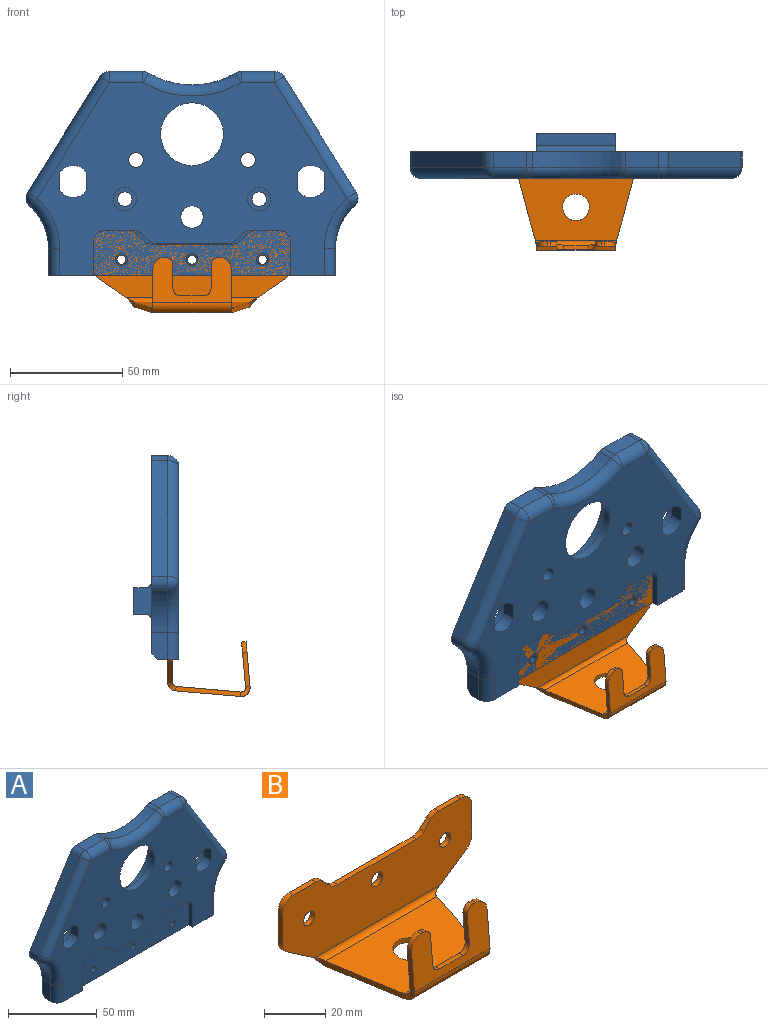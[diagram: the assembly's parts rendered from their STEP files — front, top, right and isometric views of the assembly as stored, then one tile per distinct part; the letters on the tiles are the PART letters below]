
ASSEMBLY  parts=2 mates=1
PART A: 140 faces, bbox 148.2x20x91 mm
  f0: plane 7.27x6mm, normal (-1,0,0), area 43.6mm2, adj f1,f9,f11,f79
  f1: cylinder r=7.1mm len=12.2mm, axis (0,1,0), area 88.1mm2, adj f0,f2,f11,f79
  f2: plane 7.27x6mm, normal (1,0,0), area 43.6mm2, adj f1,f9,f11,f79
  f3: cylinder r=7.1mm len=12.02mm, axis (0,1,0), area 86mm2, adj f4,f8,f11,f107
  f4: plane 7.56x6mm, normal (-1,0,0), area 45.4mm2, adj f3,f5,f11,f107
  f5: cylinder r=7.1mm len=12.02mm, axis (0,1,0), area 86mm2, adj f4,f8,f11,f107
  f6: cylinder r=3.25mm len=12mm, axis (0,1,0), area 196mm2, adj f10,f11,f89,f90,f96
  f7: cylinder r=3.25mm len=12mm, axis (0,1,0), area 196mm2, adj f10,f11,f97,f98,f105
  f8: plane 7.56x6mm, normal (1,0,0), area 45.4mm2, adj f3,f5,f11,f107
  f9: cylinder r=7.1mm len=12.2mm, axis (0,1,0), area 88.1mm2, adj f0,f2,f11,f79
  f10: plane 148.17x88.5mm, normal (0,1,0), area 4917.2mm2, adj f6,f7,f12,f13,f15,f16,f17,f19
  f11: plane 138.17x86mm, normal (0,-1,0), area 6760.8mm2, adj f0,f1,f2,f3,f4,f5,f6,f7
  f12: cylinder r=3.25mm len=6.5mm, axis (0,1,0), area 122.5mm2, adj f10,f30
  f13: cylinder r=3.25mm len=6.5mm, axis (0,1,0), area 122.5mm2, adj f10,f28
  f14: cylinder r=14mm len=28mm, axis (0,1,0), area 351.9mm2, adj f11,f26
  f15: plane 51.56x32.22mm, normal (-0.85,0,0.53), area 425.6mm2, adj f10,f31,f36,f40
  f16: cylinder r=25mm len=18.7mm, axis (0,1,0), area 147.8mm2, adj f10,f17,f31,f38
  f17: plane 12x7mm, normal (-1,0,0), area 80.9mm2, adj f10,f16,f18,f37,f59
  f18: plane 128x9.5mm, normal (0,0,-1), area 941.3mm2, adj f11,f17,f19,f37,f51,f59,f60,f61
  f19: plane 12x7mm, normal (1,0,0), area 80.9mm2, adj f10,f18,f20,f51,f59
  f20: cylinder r=25mm len=18.7mm, axis (0,1,0), area 147.8mm2, adj f10,f19,f32,f50
  f21: plane 51.56x32.22mm, normal (0.85,0,0.53), area 425.6mm2, adj f10,f32,f33,f48
  f22: plane 14.96x7mm, normal (0,0,1), area 104.7mm2, adj f10,f33,f34,f46
  f23: cylinder r=38mm len=38.72mm, axis (0,1,0), area 284.4mm2, adj f10,f34,f35,f44
  f24: plane 14.96x7mm, normal (0,0,1), area 104.7mm2, adj f10,f35,f36,f42
  f25: cylinder r=21mm len=42mm, axis (0,1,0), area 1055.6mm2, adj f10,f26
  f26: plane 42x42mm, normal (0,1,0), area 769.7mm2, adj f14,f25
  f27: cylinder r=5.25mm len=10.5mm, axis (0,-1,0), area 197.9mm2, adj f11,f28
  f28: plane 10.5x10.5mm, normal (0,-1,0), area 53.4mm2, adj f13,f27
  f29: cylinder r=5.25mm len=10.5mm, axis (0,-1,0), area 197.9mm2, adj f11,f30
  f30: plane 10.5x10.5mm, normal (0,-1,0), area 53.4mm2, adj f12,f29
  f31: cylinder r=5mm len=7mm, axis (0,1,0), area 49.1mm2, adj f10,f15,f16,f39
  f32: cylinder r=5mm len=7mm, axis (0,1,0), area 49.1mm2, adj f10,f20,f21,f49
  f33: cylinder r=5mm len=7mm, axis (0,1,0), area 35.4mm2, adj f10,f21,f22,f47
  f34: cylinder r=5mm len=7mm, axis (0,1,0), area 18.7mm2, adj f10,f22,f23,f45
  f35: cylinder r=5mm len=7mm, axis (0,1,0), area 18.7mm2, adj f10,f23,f24,f43
  f36: cylinder r=5mm len=7mm, axis (0,1,0), area 35.4mm2, adj f10,f15,f24,f41
  f37: cylinder r=5mm len=12mm, axis (0,0,1), area 94.2mm2, adj f11,f17,f18,f38
  f38: torus R=30mm, axis (0,-1,0), area 177.9mm2, adj f11,f16,f37,f39
  f39: sphere r=5mm, area 35.1mm2, adj f31,f38,f40
  f40: cylinder r=5mm len=54.21mm, axis (0.53,0,0.85), area 477.5mm2, adj f11,f15,f39,f41
  f41: sphere r=5mm, area 25.3mm2, adj f36,f40,f42
  f42: cylinder r=5mm len=14.96mm, axis (1,0,0), area 117.5mm2, adj f11,f24,f41,f43
  f43: sphere r=5mm, area 13.4mm2, adj f35,f42,f44
  f44: torus R=43mm, axis (0,-1,0), area 334.4mm2, adj f11,f23,f43,f45
  f45: sphere r=5mm, area 13.4mm2, adj f34,f44,f46
  f46: cylinder r=5mm len=14.96mm, axis (1,0,0), area 117.5mm2, adj f11,f22,f45,f47
  f47: sphere r=5mm, area 25.3mm2, adj f33,f46,f48
  f48: cylinder r=5mm len=54.21mm, axis (0.53,0,-0.85), area 477.5mm2, adj f11,f21,f47,f49
  f49: sphere r=5mm, area 35.1mm2, adj f32,f48,f50
  f50: torus R=30mm, axis (0,-1,0), area 177.9mm2, adj f11,f20,f49,f51
  f51: cylinder r=5mm len=12mm, axis (0,0,-1), area 94.2mm2, adj f11,f18,f19,f50
  f52: plane 35.5x5mm, normal (0,0,1), area 177.5mm2, adj f53,f55,f56,f58
  f53: plane 18x8mm, normal (1,0,0), area 99.9mm2, adj f10,f52,f54,f56,f57,f58
  f54: plane 35.5x5mm, normal (0,0,-1), area 177.5mm2, adj f53,f55,f56,f57
  f55: plane 18x8mm, normal (-1,0,0), area 99.9mm2, adj f10,f52,f54,f56,f57,f58
  f56: plane 35.5x12mm, normal (0,1,0), area 347.5mm2, adj f52,f53,f54,f55,f77
  f57: cylinder r=3mm len=35.5mm, axis (1,0,0), area 167.3mm2, adj f10,f53,f54,f55
  f58: cylinder r=3mm len=35.5mm, axis (-1,0,0), area 167.3mm2, adj f10,f52,f53,f55
  f59: plane 128x2.5mm, normal (0,0.71,-0.71), area 452.5mm2, adj f10,f17,f18,f19
  f60: plane 15x3mm, normal (1,0,0), area 45mm2, adj f11,f18,f67,f73
  f61: plane 15x3mm, normal (-1,0,0), area 45mm2, adj f11,f18,f67,f68
  f62: plane 12.93x3mm, normal (0,0,-1), area 38.8mm2, adj f11,f67,f68,f69
  f63: plane 3.07x3.07mm, normal (0.71,0,-0.71), area 13mm2, adj f11,f67,f69,f70
  f64: plane 31.86x3mm, normal (0,0,-1), area 95.6mm2, adj f11,f67,f70,f71
  f65: plane 3.07x3.07mm, normal (-0.71,0,-0.71), area 13mm2, adj f11,f67,f71,f72
  f66: plane 12.93x3mm, normal (0,0,-1), area 38.8mm2, adj f11,f67,f72,f73
  f67: plane 88x20mm, normal (0,-1,0), area 1459.6mm2, adj f18,f60,f61,f62,f63,f64,f65,f66
  f68: cylinder r=5mm len=5mm, axis (0,1,0), area 23.6mm2, adj f11,f61,f62,f67
  f69: cylinder r=5mm len=3.54mm, axis (0,1,0), area 11.8mm2, adj f11,f62,f63,f67
  f70: cylinder r=5mm len=3.54mm, axis (0,-1,0), area 11.8mm2, adj f11,f63,f64,f67
  f71: cylinder r=5mm len=3.54mm, axis (0,-1,0), area 11.8mm2, adj f11,f64,f65,f67
  f72: cylinder r=5mm len=3.54mm, axis (0,1,0), area 11.8mm2, adj f11,f65,f66,f67
  f73: cylinder r=5mm len=5mm, axis (0,1,0), area 23.6mm2, adj f11,f60,f66,f67
  f74: cylinder r=2mm len=9mm, axis (0,-1,0), area 113.1mm2, adj f10,f67
  f75: cylinder r=2mm len=9mm, axis (0,-1,0), area 113.1mm2, adj f10,f67
  f76: cylinder r=2mm len=9mm, axis (0,-1,0), area 113.1mm2, adj f10,f67
  f77: cylinder r=5mm len=20mm, axis (0,-1,0), area 628.3mm2, adj f11,f56
  f78: cylinder r=11.1mm len=22.2mm, axis (0,1,0), area 418.5mm2, adj f10,f79
  f79: plane 22.2x22.2mm, normal (0,1,0), area 238.5mm2, adj f0,f1,f2,f9,f78
  f80: plane 13.73x6mm, normal (1,0,0), area 82.4mm2, adj f10,f87,f116,f121
  f81: cylinder r=16mm len=6mm, axis (0,1,0), area 32.4mm2, adj f10,f87,f120,f121
  f82: plane 21.79x6mm, normal (0,0,-1), area 130.7mm2, adj f10,f87,f119,f120
  f83: plane 7.1x6mm, normal (-1,0,0), area 42.6mm2, adj f10,f87,f118,f119
  f84: plane 6x3mm, normal (0,0,1), area 18mm2, adj f10,f85,f87,f118
  f85: cylinder r=7mm len=6.64mm, axis (0,1,0), area 52.5mm2, adj f10,f84,f87,f117
  f86: plane 15.99x6mm, normal (0,0,1), area 95.9mm2, adj f10,f87,f116,f117
  f87: plane 33x18.73mm, normal (0,1,0), area 536.7mm2, adj f80,f81,f82,f83,f84,f85,f86,f116
  f88: plane 6.17x6mm, normal (0,0,1), area 37mm2, adj f10,f96,f134,f139
  f89: plane 6x4.01mm, normal (1,0,0), area 24mm2, adj f6,f10,f96,f134
  f90: plane 8.41x6mm, normal (1,0,0), area 50.4mm2, adj f6,f10,f91,f96
  f91: cylinder r=26mm len=17.31mm, axis (0,1,0), area 113.7mm2, adj f10,f90,f96,f135
  f92: plane 6x1.52mm, normal (1,0,0), area 9.1mm2, adj f10,f96,f135,f136
  f93: plane 14.22x6mm, normal (0,0,-1), area 85.3mm2, adj f10,f96,f136,f137
  f94: plane 23.34x14.58mm, normal (-0.85,0,-0.53), area 165.1mm2, adj f10,f96,f137,f138
  f95: cylinder r=16mm len=13.63mm, axis (0,1,0), area 122.5mm2, adj f10,f96,f138,f139
  f96: plane 44.1x33.8mm, normal (0,1,0), area 841.6mm2, adj f6,f88,f89,f90,f91,f92,f93,f94
  f97: plane 8.41x6mm, normal (-1,0,0), area 50.4mm2, adj f7,f10,f104,f105
  f98: plane 6x4.01mm, normal (-1,0,0), area 24mm2, adj f7,f10,f105,f133
  f99: plane 6x3.44mm, normal (0,0,1), area 20.6mm2, adj f10,f105,f132,f133
  f100: cylinder r=18.71mm len=16.08mm, axis (0,1,0), area 139.2mm2, adj f10,f105,f131,f132
  f101: plane 20.87x13.04mm, normal (0.85,0,-0.53), area 147.7mm2, adj f10,f105,f130,f131
  f102: plane 14.22x6mm, normal (0,0,-1), area 85.3mm2, adj f10,f105,f129,f130
  f103: plane 6x1.52mm, normal (-1,0,0), area 9.1mm2, adj f10,f105,f128,f129
  f104: cylinder r=26mm len=17.31mm, axis (0,1,0), area 113.7mm2, adj f10,f97,f105,f128
  f105: plane 44.1x32.26mm, normal (0,1,0), area 766.7mm2, adj f7,f97,f98,f99,f100,f101,f102,f103
  f106: cylinder r=11.1mm len=22.2mm, axis (0,1,0), area 418.5mm2, adj f10,f107
  f107: plane 22.2x22.2mm, normal (0,1,0), area 239.9mm2, adj f3,f4,f5,f8,f106
  f108: cylinder r=16mm len=6mm, axis (0,1,0), area 32.4mm2, adj f10,f115,f122,f127
  f109: plane 13.73x6mm, normal (-1,0,0), area 82.4mm2, adj f10,f115,f126,f127
  f110: plane 15.99x6mm, normal (0,0,1), area 95.9mm2, adj f10,f115,f125,f126
  f111: cylinder r=7mm len=6.64mm, axis (0,1,0), area 52.5mm2, adj f10,f112,f115,f125
  f112: plane 6x3mm, normal (0,0,1), area 18mm2, adj f10,f111,f115,f124
  f113: plane 7.1x6mm, normal (1,0,0), area 42.6mm2, adj f10,f115,f123,f124
  f114: plane 21.79x6mm, normal (0,0,-1), area 130.7mm2, adj f10,f115,f122,f123
  f115: plane 33x18.73mm, normal (0,1,0), area 536.7mm2, adj f108,f109,f110,f111,f112,f113,f114,f122
  f116: cylinder r=2.5mm len=6mm, axis (0,-1,0), area 23.6mm2, adj f10,f80,f86,f87
  f117: cylinder r=2.5mm len=6mm, axis (0,1,0), area 18.7mm2, adj f10,f85,f86,f87
  f118: cylinder r=2.5mm len=6mm, axis (0,1,0), area 23.6mm2, adj f10,f83,f84,f87
  f119: cylinder r=2.5mm len=6mm, axis (0,1,0), area 23.6mm2, adj f10,f82,f83,f87
  f120: cylinder r=2.5mm len=6mm, axis (0,1,0), area 2.2mm2, adj f10,f81,f82,f87
  f121: cylinder r=2.5mm len=6mm, axis (0,1,0), area 26.4mm2, adj f10,f80,f81,f87
  f122: cylinder r=2.5mm len=6mm, axis (0,1,0), area 2.2mm2, adj f10,f108,f114,f115
  f123: cylinder r=2.5mm len=6mm, axis (0,1,0), area 23.6mm2, adj f10,f113,f114,f115
  f124: cylinder r=2.5mm len=6mm, axis (0,1,0), area 23.6mm2, adj f10,f112,f113,f115
  f125: cylinder r=2.5mm len=6mm, axis (0,1,0), area 18.7mm2, adj f10,f110,f111,f115
  f126: cylinder r=2.5mm len=6mm, axis (0,-1,0), area 23.6mm2, adj f10,f109,f110,f115
  f127: cylinder r=2.5mm len=6mm, axis (0,1,0), area 26.4mm2, adj f10,f108,f109,f115
  f128: cylinder r=2.5mm len=6mm, axis (0,1,0), area 10.9mm2, adj f10,f103,f104,f105
  f129: cylinder r=2.5mm len=6mm, axis (0,1,0), area 23.6mm2, adj f10,f102,f103,f105
  f130: cylinder r=2.5mm len=6mm, axis (0,-1,0), area 15.2mm2, adj f10,f101,f102,f105
  f131: cylinder r=2.5mm len=6mm, axis (0,1,0), area 28.7mm2, adj f10,f100,f101,f105
  f132: cylinder r=2.5mm len=6mm, axis (0,1,0), area 21.8mm2, adj f10,f99,f100,f105
  f133: cylinder r=2.5mm len=6mm, axis (0,-1,0), area 23.6mm2, adj f10,f98,f99,f105
  f134: cylinder r=2.5mm len=6mm, axis (0,-1,0), area 23.6mm2, adj f10,f88,f89,f96
  f135: cylinder r=2.5mm len=6mm, axis (0,1,0), area 10.9mm2, adj f10,f91,f92,f96
  f136: cylinder r=2.5mm len=6mm, axis (0,-1,0), area 23.6mm2, adj f10,f92,f93,f96
  f137: cylinder r=2.5mm len=6mm, axis (0,1,0), area 15.2mm2, adj f10,f93,f94,f96
  f138: cylinder r=2.5mm len=6mm, axis (0,1,0), area 29.5mm2, adj f10,f94,f95,f96
  f139: cylinder r=2.5mm len=6mm, axis (0,1,0), area 21.5mm2, adj f10,f88,f95,f96
PART B: 50 faces, bbox 87.8x36.9x36.6 mm
  f0: plane 36.46x2mm, normal (0,0,1), area 72.9mm2, adj f12,f13,f16,f17
  f1: plane 3.14x3.14mm, normal (-0.71,0,0.71), area 8.9mm2, adj f12,f13,f15,f17
  f2: plane 10.29x2mm, normal (0,0,1), area 20.6mm2, adj f12,f13,f14,f15
  f3: plane 12.17x2mm, normal (1,0,0), area 24.3mm2, adj f12,f13,f14,f20
  f4: plane 12.66x8.68mm, normal (0.57,0,-0.82), area 30.7mm2, adj f12,f13,f20,f47
  f5: plane 12.66x8.68mm, normal (-0.57,0,-0.82), area 30.7mm2, adj f12,f13,f21,f46
  f6: plane 12.17x2mm, normal (-1,0,0), area 24.3mm2, adj f12,f13,f18,f21
  f7: plane 10.29x2mm, normal (0,0,1), area 20.6mm2, adj f12,f13,f18,f19
  f8: cylinder r=2.65mm len=5.3mm, axis (0,-1,0), area 33.3mm2, adj f12,f13
  f9: cylinder r=2.65mm len=5.3mm, axis (0,-1,0), area 33.3mm2, adj f12,f13
  f10: cylinder r=2.65mm len=5.3mm, axis (0,-1,0), area 33.3mm2, adj f12,f13
  f11: plane 3.14x3.14mm, normal (0.71,0,0.71), area 8.9mm2, adj f12,f13,f16,f19
  f12: plane 87.8x30.07mm, normal (0,1,0), area 2124.8mm2, adj f0,f1,f2,f3,f4,f5,f6,f7
  f13: plane 87.8x30.07mm, normal (0,-1,0), area 2124.8mm2, adj f0,f1,f2,f3,f4,f5,f6,f7
  f14: cylinder r=5.1mm len=5.1mm, axis (0,1,0), area 16mm2, adj f2,f3,f12,f13
  f15: cylinder r=5.1mm len=3.61mm, axis (0,1,0), area 8mm2, adj f1,f2,f12,f13
  f16: cylinder r=5mm len=3.54mm, axis (0,-1,0), area 7.9mm2, adj f0,f11,f12,f13
  f17: cylinder r=5mm len=3.54mm, axis (0,-1,0), area 7.9mm2, adj f0,f1,f12,f13
  f18: cylinder r=5.1mm len=5.1mm, axis (0,1,0), area 16mm2, adj f6,f7,f12,f13
  f19: cylinder r=5.1mm len=3.61mm, axis (0,1,0), area 8mm2, adj f7,f11,f12,f13
  f20: cylinder r=5mm len=4.12mm, axis (0,1,0), area 9.7mm2, adj f3,f4,f12,f13
  f21: cylinder r=5mm len=4.12mm, axis (0,1,0), area 9.7mm2, adj f5,f6,f12,f13
  f22: plane 29.02x7.76mm, normal (-0.97,-0.26,-0.02), area 59.9mm2, adj f25,f26,f43,f46
  f23: cylinder r=6mm len=12.13mm, axis (0,0.09,-1), area 75.4mm2, adj f25,f26
  f24: plane 29.02x7.76mm, normal (0.97,-0.26,-0.02), area 59.9mm2, adj f25,f26,f42,f47
  f25: plane 51.82x28.84mm, normal (0,0.09,-1), area 1162.5mm2, adj f22,f23,f24,f44,f48
  f26: plane 51.82x28.84mm, normal (0,-0.09,1), area 1162.5mm2, adj f22,f23,f24,f45,f49
  f27: plane 11x1.99mm, normal (0,0.09,1), area 22mm2, adj f34,f35,f38,f40
  f28: plane 11.13x2.95mm, normal (1,0,0), area 22mm2, adj f34,f35,f39,f40
  f29: plane 1.99x1.01mm, normal (0,0.09,1), area 2mm2, adj f34,f35,f37,f39
  f30: plane 15.35x3.32mm, normal (-1,0,0), area 30.5mm2, adj f34,f35,f37,f43
  f31: plane 15.35x3.32mm, normal (1,0,0), area 30.5mm2, adj f34,f35,f36,f42
  f32: plane 1.99x1.01mm, normal (0,0.09,1), area 2mm2, adj f34,f35,f36,f41
  f33: plane 11.13x2.95mm, normal (-1,0,0), area 22mm2, adj f34,f35,f38,f41
  f34: plane 35.03x20.16mm, normal (0,-1,0.09), area 408.9mm2, adj f27,f28,f29,f30,f31,f32,f33,f36
  f35: plane 35.03x20.16mm, normal (0,1,-0.09), area 408.9mm2, adj f27,f28,f29,f30,f31,f32,f33,f36
  f36: cylinder r=5mm len=5.16mm, axis (0,-1,0.09), area 15.7mm2, adj f31,f32,f34,f35
  f37: cylinder r=5mm len=5.16mm, axis (0,-1,0.09), area 15.7mm2, adj f29,f30,f34,f35
  f38: cylinder r=3mm len=3.16mm, axis (0,1,-0.09), area 9.4mm2, adj f27,f33,f34,f35
  f39: cylinder r=3mm len=3.16mm, axis (0,1,-0.09), area 9.4mm2, adj f28,f29,f34,f35
  f40: cylinder r=3mm len=3.16mm, axis (0,1,-0.09), area 9.4mm2, adj f27,f28,f34,f35
  f41: cylinder r=3mm len=3.16mm, axis (0,1,-0.09), area 9.4mm2, adj f32,f33,f34,f35
  f42: bspline ~4.38x4.36mm, area 10.6mm2, adj f24,f31,f44,f45
  f43: bspline ~4.36x4.36mm, area 10.6mm2, adj f22,f30,f44,f45
  f44: cylinder r=4mm len=36.3mm, axis (1,0,0), area 249mm2, adj f25,f34,f42,f43
  f45: cylinder r=2mm len=36.3mm, axis (1,0,0), area 124.5mm2, adj f26,f35,f42,f43
  f46: bspline ~3.98x3.83mm, area 11.3mm2, adj f5,f22,f48,f49
  f47: bspline ~3.98x3.83mm, area 11.4mm2, adj f4,f24,f48,f49
  f48: cylinder r=4mm len=58.15mm, axis (-1,0,0), area 320.5mm2, adj f12,f25,f46,f47
  f49: cylinder r=2mm len=58.15mm, axis (-1,0,0), area 160.2mm2, adj f13,f26,f46,f47
PLACE A t=(-33.6,60.19,-8.85)mm
PLACE B t=(-33.6,53.19,-56.23)mm
MATE fastened B.f9 <-> A.f75  axis (0,-1,0) through (-33.6,51.19,-53.35)mm
